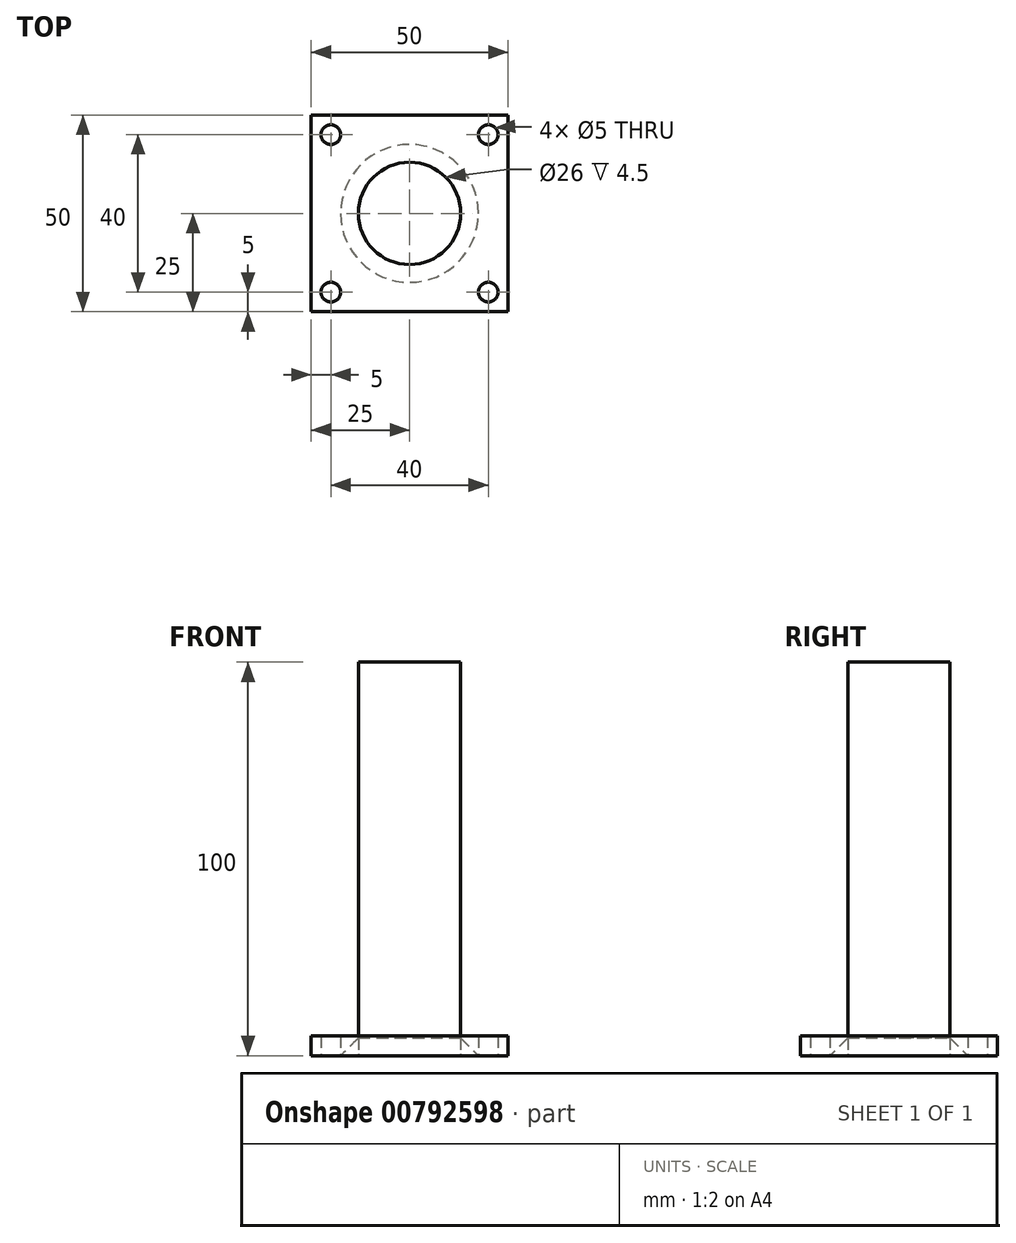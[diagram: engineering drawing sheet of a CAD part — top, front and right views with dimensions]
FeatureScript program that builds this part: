
annotation { "Feature Type Name" : "Feature", "Feature Type Description" : "" }
export const myFeature = defineFeature(function(context is Context, id is Id, definition is map)
    precondition{}
    {
        {
            var Q0;
            Q0=qCreatedBy(makeId("Top.planeOp"),FACE);
            var sketch = newSketch(context, id + "F0", { "sketchPlane" : qUnion([Q0])});
            skCircle(sketch, "E0", {"center": v(0, 0) * mm, "radius": 13 * mm});
            skSolve(sketch);
        }
        {
            var Q0;
            Q0 = qSketchRegion(id + "F0", true);
            extrude(context, id + "F1", {"entities" : qUnion([Q0]), "depth" : 100 * mm, "offsetDistance" : 25 * mm});
        }
        {
            var Q0;
            Q0=qCreatedBy(makeId("Top.planeOp"),FACE);
            var sketch = newSketch(context, id + "F2", { "sketchPlane" : qUnion([Q0])});
            skLineSegment(sketch, "E1.bottom", {"start": v(25, 25) * mm, "end": v(-25, 25) * mm});
            skLineSegment(sketch, "E1.top", {"start": v(25, -25) * mm, "end": v(-25, -25) * mm});
            skLineSegment(sketch, "E1.left", {"start": v(25, 25) * mm, "end": v(25, -25) * mm});
            skLineSegment(sketch, "E1.right", {"start": v(-25, 25) * mm, "end": v(-25, -25) * mm});
            skPoint(sketch, "E1.middle", {"position": v(0, 0) * mm});
            skCircle(sketch, "E2", {"center": v(-20, 20) * mm, "radius": 2.5 * mm});
            skCircle(sketch, "E3", {"center": v(20, 20) * mm, "radius": 2.5 * mm});
            skCircle(sketch, "E4", {"center": v(-20, -20) * mm, "radius": 2.5 * mm});
            skCircle(sketch, "E5", {"center": v(20, -20) * mm, "radius": 2.5 * mm});
            skSolve(sketch);
        }
        {
            var Q0;
            Q0 = qSketchRegion(id + "F2", true);
            extrude(context, id + "F3", {"entities" : qUnion([Q0]), "depth" : 5 * mm, "offsetDistance" : 25 * mm});
        }
        {
            var Q0;
            Q0=qCreatedBy(makeId("Top.planeOp"),FACE);
            var sketch = newSketch(context, id + "F4", { "sketchPlane" : qUnion([Q0])});
            skCircle(sketch, "E6", {"center": v(0, 0) * mm, "radius": 13 * mm});
            skCircle(sketch, "E7", {"center": v(0, 0) * mm, "radius": 17.5 * mm});
            skSolve(sketch);
        }
        {
            var Q0;
            Q0 = qSketchRegion(id + "F4", true);
            extrude(context, id + "F5", {"entities" : qUnion([Q0]), "depth" : 5 * mm, "offsetDistance" : 25 * mm});
        }
        {
            var Q0;
            Q0=makeQuery(id+"F5.opExtrude","CAP_EDGE",EDGE,{"disambiguationData":[OSD([sQuery(id+"F4.wireOp",EDGE,"E7")])],"isStart":false});
            chamfer(context, id + "F6", {"entities" : qUnion([Q0]), "width" : 5 * mm, "tangentPropagation" : true});
        }
    });
